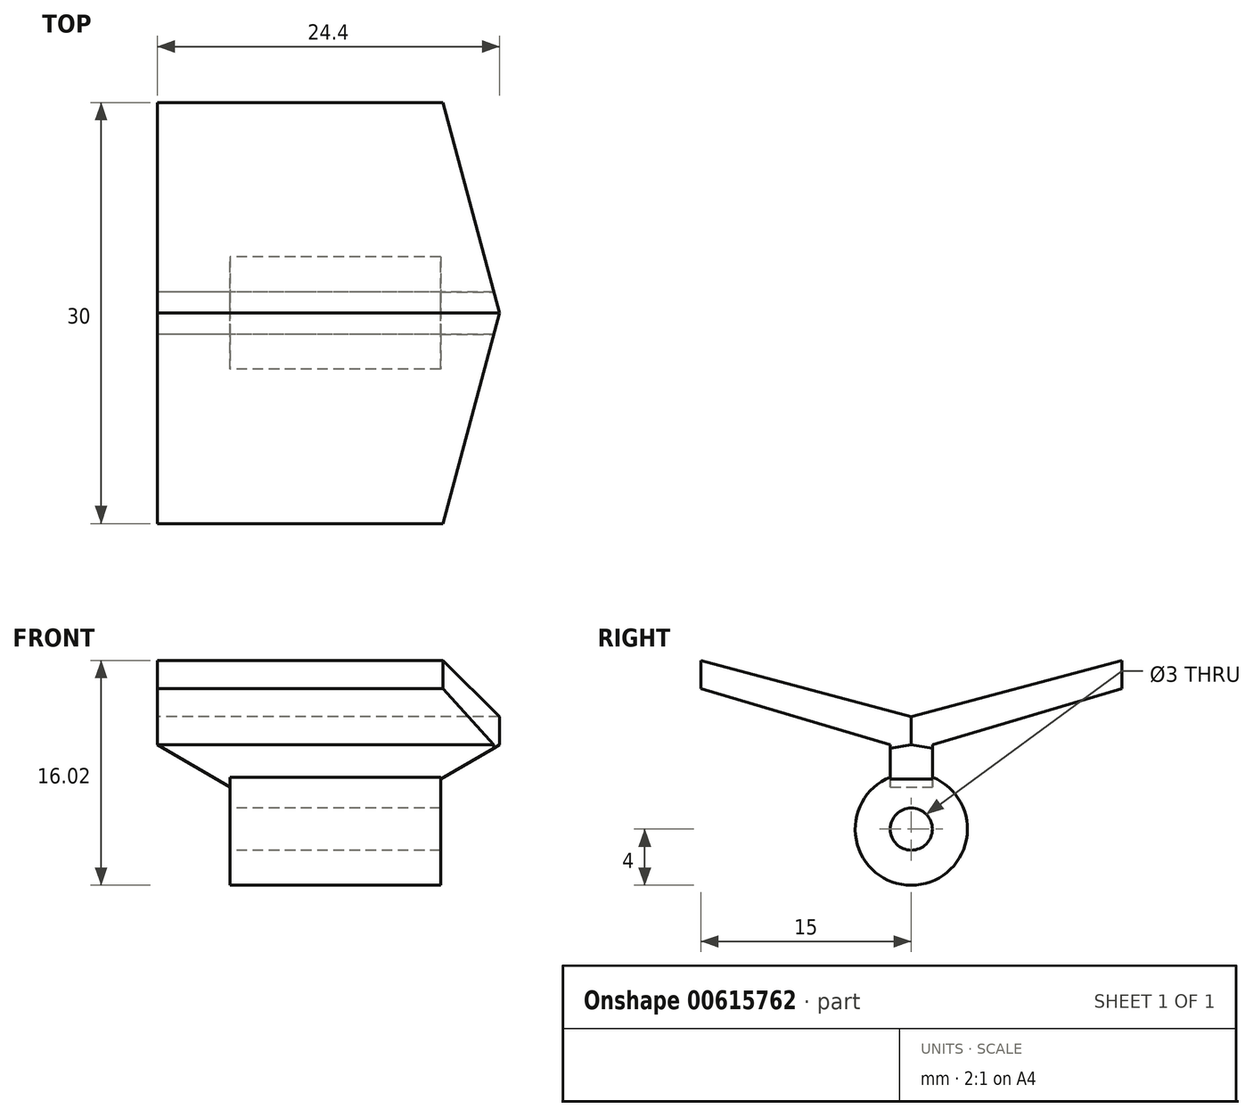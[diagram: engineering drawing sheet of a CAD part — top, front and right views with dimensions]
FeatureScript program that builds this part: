
annotation { "Feature Type Name" : "Feature", "Feature Type Description" : "" }
export const myFeature = defineFeature(function(context is Context, id is Id, definition is map)
    precondition{}
    {
        {
            var Q0;
            Q0=qCreatedBy(makeId("Right.planeOp"),FACE);
            var sketch = newSketch(context, id + "F0", { "sketchPlane" : qUnion([Q0])});
            skCircle(sketch, "E0", {"center": v(0, 0) * mm, "radius": 1.5 * mm});
            skCircle(sketch, "E1", {"center": v(0, 0) * mm, "radius": 4 * mm});
            skSolve(sketch);
        }
        {
            var Q0;
            Q0=makeQuery(id+"F0.imprint","IMPRINT",FACE,{"disambiguationData":[TD([[makeQuery(id+"F0.imprint","IMPRINT",EDGE,{"derivedFrom":sQuery(id+"F0.wireOp",EDGE,"E0")}),-1.0]])]});
            var Q1;
            Q1=qConstructionFilter(qBodyType(qCreatedBy(id+"F0",EDGE),BodyType.WIRE),ConstructionObject.NO);
            extrude(context, id + "F1", {"entities" : qUnion([Q0]), "surfaceEntities" : qUnion([Q1]), "depth" : 15 * mm, "offsetDistance" : 25 * mm});
        }
        {
            var Q0;
            Q0=qCreatedBy(makeId("Front.planeOp"),FACE);
            var sketch = newSketch(context, id + "F2", { "sketchPlane" : qUnion([Q0])});
            skLineSegment(sketch, "E2", {"start": v(0, 3) * mm, "end": v(14, 3) * mm});
            skLineSegment(sketch, "E3", {"start": v(0, 3) * mm, "end": v(-5.2, 6) * mm});
            skLineSegment(sketch, "E4", {"start": v(14, 3) * mm, "end": v(19.2, 6) * mm});
            skLineSegment(sketch, "E5", {"start": v(-5.2, 6) * mm, "end": v(-5.2, 8) * mm});
            skLineSegment(sketch, "E6", {"start": v(-5.2, 8) * mm, "end": v(19.2, 8) * mm});
            skLineSegment(sketch, "E7", {"start": v(19.2, 8) * mm, "end": v(19.2, 6) * mm});
            skSolve(sketch);
        }
        {
            var Q0;
            Q0 = qSketchRegion(id + "F2", true);
            extrude(context, id + "F3", {"entities" : qUnion([Q0]), "operationType" : NewBodyOperationType.ADD, "endBound" : BoundingType.SYMMETRIC, "depth" : 3 * mm, "offsetDistance" : 25 * mm});
        }
        {
            var Q0;
            Q0=makeQuery(id+"F3.opExtrude","SWEPT_FACE",FACE,{"disambiguationData":[OSD([sQuery(id+"F2.wireOp",EDGE,"E5")])]});
            var sketch = newSketch(context, id + "F4", { "sketchPlane" : qUnion([Q0])});
            skLineSegment(sketch, "E8", {"start": v(0, 8) * mm, "end": v(0, 13) * mm, "construction": true});
            skPoint(sketch, "E8.endSnap0", {"position": v(0, 8) * mm});
            skLineSegment(sketch, "E9", {"start": v(0, 8) * mm, "end": v(15, 12.02) * mm});
            skLineSegment(sketch, "E10", {"start": v(0, 8) * mm, "end": v(10.53, 8) * mm, "construction": true});
            skLineSegment(sketch, "E11", {"start": v(15, 12.02) * mm, "end": v(15, 10.02) * mm});
            skLineSegment(sketch, "E12", {"start": v(15, 10.02) * mm, "end": v(1.5, 6) * mm});
            skLineSegment(sketch, "E13", {"start": v(1.5, 6) * mm, "end": v(0, 8) * mm});
            skLineSegment(sketch, "E14.MirrorCS", {"start": v(0, 8) * mm, "end": v(-15, 12.02) * mm});
            skLineSegment(sketch, "E15.MirrorCS", {"start": v(-1.5, 6) * mm, "end": v(0, 8) * mm});
            skLineSegment(sketch, "E16.MirrorCS", {"start": v(-15, 10.02) * mm, "end": v(-1.5, 6) * mm});
            skLineSegment(sketch, "E17.MirrorCS", {"start": v(-15, 12.02) * mm, "end": v(-15, 10.02) * mm});
            skSolve(sketch);
        }
        {
            var Q0;
            Q0 = qSketchRegion(id + "F4", true);
            var Q1;
            Q1=makeQuery(id+"F3.opExtrude","SWEPT_FACE",FACE,{"disambiguationData":[OSD([sQuery(id+"F2.wireOp",EDGE,"E7")])]});
            extrude(context, id + "F5", {"entities" : qUnion([Q0]), "operationType" : NewBodyOperationType.ADD, "endBound" : BoundingType.UP_TO_SURFACE, "oppositeDirection" : true, "depth" : 25 * mm, "endBoundEntityFace" : qUnion([Q1]), "offsetDistance" : 25 * mm});
        }
        {
            var Q0;
            Q0=qCreatedBy(makeId("Top.planeOp"),FACE);
            var sketch = newSketch(context, id + "F6", { "sketchPlane" : qUnion([Q0])});
            skLineSegment(sketch, "E18", {"start": v(0, 0) * mm, "end": v(37.12, 0) * mm, "construction": true});
            skLineSegment(sketch, "E19.0", {"start": v(19.2, 0) * mm, "end": v(19.2, -15) * mm, "construction": true});
            skLineSegment(sketch, "E20", {"start": v(19.2, 0) * mm, "end": v(14.14, -18.88) * mm});
            skLineSegment(sketch, "E21", {"start": v(14.14, -18.88) * mm, "end": v(27.25, -18.88) * mm});
            skLineSegment(sketch, "E22", {"start": v(27.25, -18.88) * mm, "end": v(27.25, 0) * mm});
            skLineSegment(sketch, "E23.MirrorCS", {"start": v(19.2, 0) * mm, "end": v(14.14, 18.88) * mm});
            skLineSegment(sketch, "E24.MirrorCS", {"start": v(14.14, 18.88) * mm, "end": v(27.25, 18.88) * mm});
            skLineSegment(sketch, "E25.MirrorCS", {"start": v(27.25, 18.88) * mm, "end": v(27.25, 0) * mm});
            skSolve(sketch);
        }
        {
            var Q0;
            Q0 = qSketchRegion(id + "F6", true);
            extrude(context, id + "F7", {"entities" : qUnion([Q0]), "operationType" : NewBodyOperationType.REMOVE, "depth" : 25 * mm, "offsetDistance" : 25 * mm});
        }
    });
